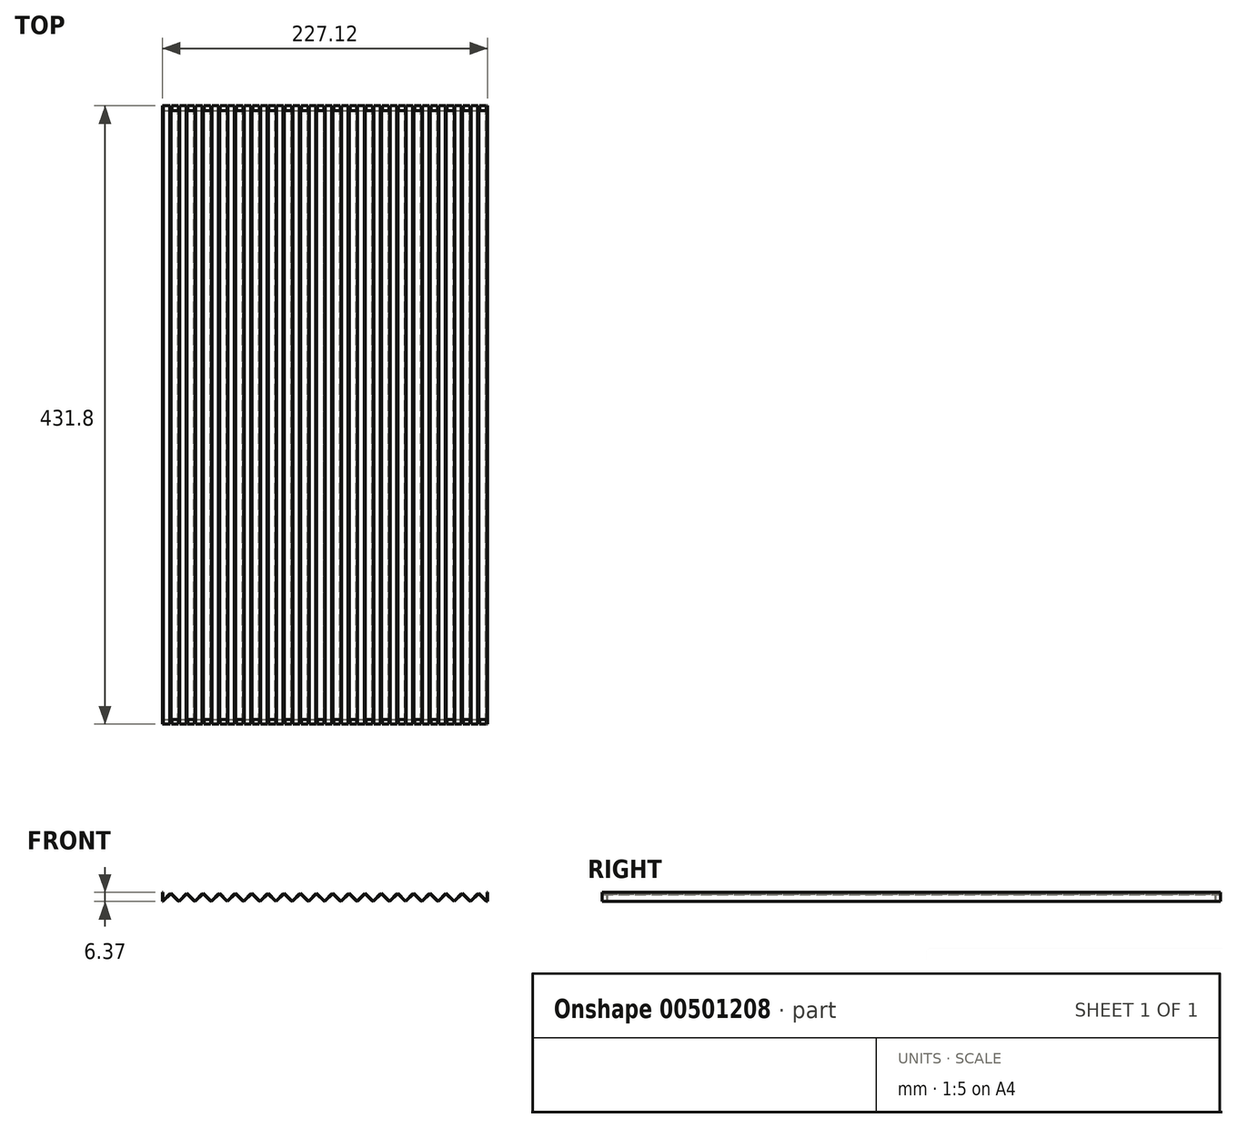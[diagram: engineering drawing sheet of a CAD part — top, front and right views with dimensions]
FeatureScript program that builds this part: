
annotation { "Feature Type Name" : "Feature", "Feature Type Description" : "" }
export const myFeature = defineFeature(function(context is Context, id is Id, definition is map)
    precondition{}
    {
        {
            assignVariable(context, id + "F0", {"variableType" : VariableType.LENGTH, "name" : "StripL", "lengthValue" : 431.8 * mm});
        }
        {
            var Q0;
            Q0=qCreatedBy(makeId("Front.planeOp"),FACE);
            var sketch = newSketch(context, id + "F1", { "sketchPlane" : qUnion([Q0])});
            skLineSegment(sketch, "E0", {"start": v(-11.31, 2.85) * mm, "end": v(0, 2.85) * mm, "construction": true});
            skLineSegment(sketch, "E1", {"start": v(-11.31, -2.85) * mm, "end": v(0, -2.85) * mm, "construction": true});
            skLineSegment(sketch, "E2", {"start": v(-11.31, -2.85) * mm, "end": v(-5.66, 2.81) * mm});
            skLineSegment(sketch, "E3", {"start": v(-5.66, 2.81) * mm, "end": v(0, -2.85) * mm});
            skLineSegment(sketch, "E4", {"start": v(-11.31, -2.81) * mm, "end": v(-5.66, 2.85) * mm});
            skLineSegment(sketch, "E5", {"start": v(-5.66, 2.85) * mm, "end": v(0, -2.81) * mm});
            skLineSegment(sketch, "E6.1.0.0", {"start": v(0, -2.81) * mm, "end": v(5.66, 2.85) * mm});
            skLineSegment(sketch, "E6.1.0.1", {"start": v(0, -2.85) * mm, "end": v(5.66, 2.81) * mm});
            skLineSegment(sketch, "E6.1.0.2", {"start": v(5.66, 2.81) * mm, "end": v(11.31, -2.85) * mm});
            skLineSegment(sketch, "E6.1.0.3", {"start": v(5.66, 2.85) * mm, "end": v(11.31, -2.81) * mm});
            skLineSegment(sketch, "E6.2.0.0", {"start": v(11.31, -2.81) * mm, "end": v(16.97, 2.85) * mm});
            skLineSegment(sketch, "E6.2.0.1", {"start": v(11.31, -2.85) * mm, "end": v(16.97, 2.81) * mm});
            skLineSegment(sketch, "E6.2.0.2", {"start": v(16.97, 2.81) * mm, "end": v(22.63, -2.85) * mm});
            skLineSegment(sketch, "E6.2.0.3", {"start": v(16.97, 2.85) * mm, "end": v(22.63, -2.81) * mm});
            skLineSegment(sketch, "E6.direction1", {"start": v(-11.31, -2.81) * mm, "end": v(0, -2.81) * mm, "construction": true});
            skLineSegment(sketch, "E7.0.3.0", {"start": v(22.63, -2.81) * mm, "end": v(28.28, 2.85) * mm});
            skLineSegment(sketch, "E7.3.3.0", {"start": v(22.63, -2.85) * mm, "end": v(28.28, 2.81) * mm});
            skLineSegment(sketch, "E7.6.3.0", {"start": v(28.28, 2.81) * mm, "end": v(33.94, -2.85) * mm});
            skLineSegment(sketch, "E7.9.3.0", {"start": v(28.28, 2.85) * mm, "end": v(33.94, -2.81) * mm});
            skLineSegment(sketch, "E7.0.4.0", {"start": v(33.94, -2.81) * mm, "end": v(39.6, 2.85) * mm});
            skLineSegment(sketch, "E7.3.4.0", {"start": v(33.94, -2.85) * mm, "end": v(39.6, 2.81) * mm});
            skLineSegment(sketch, "E7.6.4.0", {"start": v(39.6, 2.81) * mm, "end": v(45.25, -2.85) * mm});
            skLineSegment(sketch, "E7.9.4.0", {"start": v(39.6, 2.85) * mm, "end": v(45.25, -2.81) * mm});
            skLineSegment(sketch, "E8.0.5.0", {"start": v(45.25, -2.81) * mm, "end": v(50.91, 2.85) * mm});
            skLineSegment(sketch, "E8.3.5.0", {"start": v(45.25, -2.85) * mm, "end": v(50.91, 2.81) * mm});
            skLineSegment(sketch, "E8.6.5.0", {"start": v(50.91, 2.81) * mm, "end": v(56.57, -2.85) * mm});
            skLineSegment(sketch, "E8.9.5.0", {"start": v(50.91, 2.85) * mm, "end": v(56.57, -2.81) * mm});
            skLineSegment(sketch, "E9.0.6.0", {"start": v(56.57, -2.81) * mm, "end": v(62.23, 2.85) * mm});
            skLineSegment(sketch, "E9.3.6.0", {"start": v(56.57, -2.85) * mm, "end": v(62.23, 2.81) * mm});
            skLineSegment(sketch, "E9.6.6.0", {"start": v(62.23, 2.81) * mm, "end": v(67.88, -2.85) * mm});
            skLineSegment(sketch, "E9.9.6.0", {"start": v(62.23, 2.85) * mm, "end": v(67.88, -2.81) * mm});
            skLineSegment(sketch, "E9.0.7.0", {"start": v(67.88, -2.81) * mm, "end": v(73.54, 2.85) * mm});
            skLineSegment(sketch, "E9.3.7.0", {"start": v(67.88, -2.85) * mm, "end": v(73.54, 2.81) * mm});
            skLineSegment(sketch, "E9.6.7.0", {"start": v(73.54, 2.81) * mm, "end": v(79.2, -2.85) * mm});
            skLineSegment(sketch, "E9.9.7.0", {"start": v(73.54, 2.85) * mm, "end": v(79.2, -2.81) * mm});
            skLineSegment(sketch, "E10.0.8.0", {"start": v(79.2, -2.81) * mm, "end": v(84.85, 2.85) * mm});
            skLineSegment(sketch, "E10.3.8.0", {"start": v(79.2, -2.85) * mm, "end": v(84.85, 2.81) * mm});
            skLineSegment(sketch, "E10.6.8.0", {"start": v(84.85, 2.81) * mm, "end": v(90.5, -2.85) * mm});
            skLineSegment(sketch, "E10.9.8.0", {"start": v(84.85, 2.85) * mm, "end": v(90.5, -2.81) * mm});
            skLineSegment(sketch, "E10.0.9.0", {"start": v(90.5, -2.81) * mm, "end": v(96.17, 2.85) * mm});
            skLineSegment(sketch, "E10.3.9.0", {"start": v(90.5, -2.85) * mm, "end": v(96.17, 2.81) * mm});
            skLineSegment(sketch, "E10.6.9.0", {"start": v(96.17, 2.81) * mm, "end": v(101.82, -2.85) * mm});
            skLineSegment(sketch, "E10.9.9.0", {"start": v(96.17, 2.85) * mm, "end": v(101.82, -2.81) * mm});
            skLineSegment(sketch, "E10.0.10.0", {"start": v(101.82, -2.81) * mm, "end": v(107.48, 2.85) * mm});
            skLineSegment(sketch, "E10.3.10.0", {"start": v(101.82, -2.85) * mm, "end": v(107.48, 2.81) * mm});
            skLineSegment(sketch, "E10.6.10.0", {"start": v(107.48, 2.81) * mm, "end": v(113.14, -2.85) * mm});
            skLineSegment(sketch, "E10.9.10.0", {"start": v(107.48, 2.85) * mm, "end": v(113.14, -2.81) * mm});
            skLineSegment(sketch, "E10.0.11.0", {"start": v(113.14, -2.81) * mm, "end": v(118.8, 2.85) * mm});
            skLineSegment(sketch, "E10.3.11.0", {"start": v(113.14, -2.85) * mm, "end": v(118.8, 2.81) * mm});
            skLineSegment(sketch, "E10.6.11.0", {"start": v(118.8, 2.81) * mm, "end": v(124.45, -2.85) * mm});
            skLineSegment(sketch, "E10.9.11.0", {"start": v(118.8, 2.85) * mm, "end": v(124.45, -2.81) * mm});
            skLineSegment(sketch, "E10.0.12.0", {"start": v(124.45, -2.81) * mm, "end": v(130.1, 2.85) * mm});
            skLineSegment(sketch, "E10.3.12.0", {"start": v(124.45, -2.85) * mm, "end": v(130.1, 2.81) * mm});
            skLineSegment(sketch, "E10.6.12.0", {"start": v(130.1, 2.81) * mm, "end": v(135.76, -2.85) * mm});
            skLineSegment(sketch, "E10.9.12.0", {"start": v(130.1, 2.85) * mm, "end": v(135.76, -2.81) * mm});
            skLineSegment(sketch, "E10.0.13.0", {"start": v(135.76, -2.81) * mm, "end": v(141.42, 2.85) * mm});
            skLineSegment(sketch, "E10.3.13.0", {"start": v(135.76, -2.85) * mm, "end": v(141.42, 2.81) * mm});
            skLineSegment(sketch, "E10.6.13.0", {"start": v(141.42, 2.81) * mm, "end": v(147.08, -2.85) * mm});
            skLineSegment(sketch, "E10.9.13.0", {"start": v(141.42, 2.85) * mm, "end": v(147.08, -2.81) * mm});
            skLineSegment(sketch, "E10.0.14.0", {"start": v(147.08, -2.81) * mm, "end": v(152.74, 2.85) * mm});
            skLineSegment(sketch, "E10.3.14.0", {"start": v(147.08, -2.85) * mm, "end": v(152.74, 2.81) * mm});
            skLineSegment(sketch, "E10.6.14.0", {"start": v(152.74, 2.81) * mm, "end": v(158.4, -2.85) * mm});
            skLineSegment(sketch, "E10.9.14.0", {"start": v(152.74, 2.85) * mm, "end": v(158.4, -2.81) * mm});
            skLineSegment(sketch, "E10.0.15.0", {"start": v(158.4, -2.81) * mm, "end": v(164.05, 2.85) * mm});
            skLineSegment(sketch, "E10.3.15.0", {"start": v(158.4, -2.85) * mm, "end": v(164.05, 2.81) * mm});
            skLineSegment(sketch, "E10.6.15.0", {"start": v(164.05, 2.81) * mm, "end": v(169.7, -2.85) * mm});
            skLineSegment(sketch, "E10.9.15.0", {"start": v(164.05, 2.85) * mm, "end": v(169.7, -2.81) * mm});
            skLineSegment(sketch, "E10.0.16.0", {"start": v(169.7, -2.81) * mm, "end": v(175.36, 2.85) * mm});
            skLineSegment(sketch, "E10.3.16.0", {"start": v(169.7, -2.85) * mm, "end": v(175.36, 2.81) * mm});
            skLineSegment(sketch, "E10.6.16.0", {"start": v(175.36, 2.81) * mm, "end": v(181.02, -2.85) * mm});
            skLineSegment(sketch, "E10.9.16.0", {"start": v(175.36, 2.85) * mm, "end": v(181.02, -2.81) * mm});
            skLineSegment(sketch, "E10.0.17.0", {"start": v(181.02, -2.81) * mm, "end": v(186.68, 2.85) * mm});
            skLineSegment(sketch, "E10.3.17.0", {"start": v(181.02, -2.85) * mm, "end": v(186.68, 2.81) * mm});
            skLineSegment(sketch, "E10.6.17.0", {"start": v(186.68, 2.81) * mm, "end": v(192.33, -2.85) * mm});
            skLineSegment(sketch, "E10.9.17.0", {"start": v(186.68, 2.85) * mm, "end": v(192.33, -2.81) * mm});
            skLineSegment(sketch, "E10.0.18.0", {"start": v(192.33, -2.81) * mm, "end": v(197.99, 2.85) * mm});
            skLineSegment(sketch, "E10.3.18.0", {"start": v(192.33, -2.85) * mm, "end": v(197.99, 2.81) * mm});
            skLineSegment(sketch, "E10.6.18.0", {"start": v(197.99, 2.81) * mm, "end": v(203.65, -2.85) * mm});
            skLineSegment(sketch, "E10.9.18.0", {"start": v(197.99, 2.85) * mm, "end": v(203.65, -2.81) * mm});
            skLineSegment(sketch, "E10.0.19.0", {"start": v(203.65, -2.81) * mm, "end": v(209.3, 2.85) * mm});
            skLineSegment(sketch, "E10.3.19.0", {"start": v(203.65, -2.85) * mm, "end": v(209.3, 2.81) * mm});
            skLineSegment(sketch, "E10.6.19.0", {"start": v(209.3, 2.81) * mm, "end": v(214.96, -2.85) * mm});
            skLineSegment(sketch, "E10.9.19.0", {"start": v(209.3, 2.85) * mm, "end": v(214.96, -2.81) * mm});
            skLineSegment(sketch, "E11", {"start": v(-11.31, -2.81) * mm, "end": v(-11.31, 2.85) * mm});
            skLineSegment(sketch, "E12", {"start": v(-11.31, -2.85) * mm, "end": v(-11.33, -2.83) * mm});
            skLineSegment(sketch, "E13", {"start": v(-11.33, -2.83) * mm, "end": v(-11.33, 2.85) * mm});
            skLineSegment(sketch, "E14", {"start": v(-11.33, 2.85) * mm, "end": v(-11.31, 2.85) * mm});
            skLineSegment(sketch, "E15", {"start": v(214.96, -2.81) * mm, "end": v(214.96, 2.85) * mm});
            skLineSegment(sketch, "E16", {"start": v(214.96, -2.85) * mm, "end": v(214.98, -2.83) * mm});
            skLineSegment(sketch, "E17", {"start": v(214.98, -2.83) * mm, "end": v(214.98, 2.85) * mm});
            skLineSegment(sketch, "E18", {"start": v(214.98, 2.85) * mm, "end": v(214.96, 2.85) * mm});
            skSolve(sketch);
        }
        {
            var Q0;
            Q0 = qSketchRegion(id + "F1", true);
            extrude(context, id + "F2", {"entities" : qUnion([Q0]), "depth" : 425 * mm, "offsetDistance" : 25 * mm, "symmetric" : true});
        }
        {
            var Q0;
            Q0=qCreatedBy(makeId("Front.planeOp"),FACE);
            var sketch = newSketch(context, id + "F3", { "sketchPlane" : qUnion([Q0])});
            skLineSegment(sketch, "E19.0", {"start": v(-11.33, -2.83) * mm, "end": v(-11.33, 2.85) * mm});
            skLineSegment(sketch, "E19.1", {"start": v(-11.31, -2.81) * mm, "end": v(-5.66, 2.85) * mm});
            skLineSegment(sketch, "E19.2", {"start": v(-5.66, 2.81) * mm, "end": v(0, -2.85) * mm});
            skLineSegment(sketch, "E19.3", {"start": v(0, -2.81) * mm, "end": v(5.66, 2.85) * mm});
            skLineSegment(sketch, "E19.4", {"start": v(5.66, 2.81) * mm, "end": v(11.31, -2.85) * mm});
            skLineSegment(sketch, "E19.5", {"start": v(11.31, -2.81) * mm, "end": v(16.97, 2.85) * mm});
            skLineSegment(sketch, "E19.6", {"start": v(16.97, 2.81) * mm, "end": v(22.63, -2.85) * mm});
            skLineSegment(sketch, "E19.7", {"start": v(22.63, -2.81) * mm, "end": v(28.28, 2.85) * mm});
            skLineSegment(sketch, "E19.8", {"start": v(28.28, 2.81) * mm, "end": v(33.94, -2.85) * mm});
            skLineSegment(sketch, "E19.9", {"start": v(33.94, -2.81) * mm, "end": v(39.6, 2.85) * mm});
            skLineSegment(sketch, "E19.10", {"start": v(39.6, 2.81) * mm, "end": v(45.25, -2.85) * mm});
            skLineSegment(sketch, "E19.11", {"start": v(45.25, -2.81) * mm, "end": v(50.91, 2.85) * mm});
            skLineSegment(sketch, "E19.12", {"start": v(50.91, 2.81) * mm, "end": v(56.57, -2.85) * mm});
            skLineSegment(sketch, "E19.13", {"start": v(56.57, -2.81) * mm, "end": v(62.23, 2.85) * mm});
            skLineSegment(sketch, "E19.14", {"start": v(62.23, 2.81) * mm, "end": v(67.88, -2.85) * mm});
            skLineSegment(sketch, "E19.15", {"start": v(67.88, -2.81) * mm, "end": v(73.54, 2.85) * mm});
            skLineSegment(sketch, "E19.16", {"start": v(73.54, 2.81) * mm, "end": v(79.2, -2.85) * mm});
            skLineSegment(sketch, "E19.17", {"start": v(79.2, -2.81) * mm, "end": v(84.85, 2.85) * mm});
            skLineSegment(sketch, "E19.18", {"start": v(84.85, 2.81) * mm, "end": v(90.5, -2.85) * mm});
            skLineSegment(sketch, "E19.19", {"start": v(90.5, -2.81) * mm, "end": v(96.17, 2.85) * mm});
            skLineSegment(sketch, "E19.20", {"start": v(96.17, 2.81) * mm, "end": v(101.82, -2.85) * mm});
            skLineSegment(sketch, "E19.21", {"start": v(101.82, -2.81) * mm, "end": v(107.48, 2.85) * mm});
            skLineSegment(sketch, "E19.22", {"start": v(107.48, 2.81) * mm, "end": v(113.14, -2.85) * mm});
            skLineSegment(sketch, "E19.23", {"start": v(113.14, -2.81) * mm, "end": v(118.8, 2.85) * mm});
            skLineSegment(sketch, "E19.24", {"start": v(118.8, 2.81) * mm, "end": v(124.45, -2.85) * mm});
            skLineSegment(sketch, "E19.25", {"start": v(124.45, -2.81) * mm, "end": v(130.1, 2.85) * mm});
            skLineSegment(sketch, "E19.26", {"start": v(130.1, 2.81) * mm, "end": v(135.76, -2.85) * mm});
            skLineSegment(sketch, "E19.27", {"start": v(135.76, -2.81) * mm, "end": v(141.42, 2.85) * mm});
            skLineSegment(sketch, "E19.28", {"start": v(141.42, 2.81) * mm, "end": v(147.08, -2.85) * mm});
            skLineSegment(sketch, "E19.29", {"start": v(147.08, -2.81) * mm, "end": v(152.74, 2.85) * mm});
            skLineSegment(sketch, "E19.30", {"start": v(152.74, 2.81) * mm, "end": v(158.4, -2.85) * mm});
            skLineSegment(sketch, "E19.31", {"start": v(158.4, -2.81) * mm, "end": v(164.05, 2.85) * mm});
            skLineSegment(sketch, "E19.32", {"start": v(164.05, 2.81) * mm, "end": v(169.7, -2.85) * mm});
            skLineSegment(sketch, "E19.33", {"start": v(169.7, -2.81) * mm, "end": v(175.36, 2.85) * mm});
            skLineSegment(sketch, "E19.34", {"start": v(175.36, 2.81) * mm, "end": v(181.02, -2.85) * mm});
            skLineSegment(sketch, "E19.35", {"start": v(181.02, -2.81) * mm, "end": v(186.68, 2.85) * mm});
            skLineSegment(sketch, "E19.36", {"start": v(186.68, 2.81) * mm, "end": v(192.33, -2.85) * mm});
            skLineSegment(sketch, "E19.37", {"start": v(192.33, -2.81) * mm, "end": v(197.99, 2.85) * mm});
            skLineSegment(sketch, "E19.38", {"start": v(197.99, 2.81) * mm, "end": v(203.65, -2.85) * mm});
            skLineSegment(sketch, "E19.39", {"start": v(203.65, -2.81) * mm, "end": v(209.3, 2.85) * mm});
            skLineSegment(sketch, "E19.40", {"start": v(209.3, 2.81) * mm, "end": v(214.96, -2.85) * mm});
            skLineSegment(sketch, "E19.41", {"start": v(214.96, -2.81) * mm, "end": v(214.96, 2.85) * mm});
            skLineSegment(sketch, "E20", {"start": v(-10.73, -2.23) * mm, "end": v(-11.02, -1.94) * mm});
            skLineSegment(sketch, "E21", {"start": v(-11.02, -1.94) * mm, "end": v(-6.53, 2.55) * mm});
            skLineSegment(sketch, "E22", {"start": v(-6.53, 2.55) * mm, "end": v(-6.24, 2.26) * mm});
            skLineSegment(sketch, "E23", {"start": v(-8.77, 0.3) * mm, "end": v(-8.49, 0.02) * mm, "construction": true});
            skLineSegment(sketch, "E24", {"start": v(-5.07, 2.23) * mm, "end": v(-5.36, 1.94) * mm});
            skLineSegment(sketch, "E25", {"start": v(-5.36, 1.94) * mm, "end": v(-0.87, -2.55) * mm});
            skLineSegment(sketch, "E26", {"start": v(-0.87, -2.55) * mm, "end": v(-0.58, -2.26) * mm});
            skLineSegment(sketch, "E27", {"start": v(-3.12, -0.3) * mm, "end": v(-2.83, -0.02) * mm, "construction": true});
            skLineSegment(sketch, "E28.1.0.0", {"start": v(4.79, 2.55) * mm, "end": v(5.07, 2.26) * mm});
            skLineSegment(sketch, "E28.1.0.1", {"start": v(0.3, -1.94) * mm, "end": v(4.79, 2.55) * mm});
            skLineSegment(sketch, "E28.1.0.2", {"start": v(0.58, -2.23) * mm, "end": v(0.3, -1.94) * mm});
            skLineSegment(sketch, "E28.1.0.3", {"start": v(6.24, 2.23) * mm, "end": v(5.95, 1.94) * mm});
            skLineSegment(sketch, "E28.1.0.4", {"start": v(5.95, 1.94) * mm, "end": v(10.44, -2.55) * mm});
            skLineSegment(sketch, "E28.1.0.5", {"start": v(10.44, -2.55) * mm, "end": v(10.73, -2.26) * mm});
            skLineSegment(sketch, "E28.2.0.0", {"start": v(16.1, 2.55) * mm, "end": v(16.39, 2.26) * mm});
            skLineSegment(sketch, "E28.2.0.1", {"start": v(11.6, -1.94) * mm, "end": v(16.1, 2.55) * mm});
            skLineSegment(sketch, "E28.2.0.2", {"start": v(11.9, -2.23) * mm, "end": v(11.6, -1.94) * mm});
            skLineSegment(sketch, "E28.2.0.3", {"start": v(17.55, 2.23) * mm, "end": v(17.27, 1.94) * mm});
            skLineSegment(sketch, "E28.2.0.4", {"start": v(17.27, 1.94) * mm, "end": v(21.76, -2.55) * mm});
            skLineSegment(sketch, "E28.2.0.5", {"start": v(21.76, -2.55) * mm, "end": v(22.04, -2.26) * mm});
            skLineSegment(sketch, "E28.3.0.0", {"start": v(27.41, 2.55) * mm, "end": v(27.7, 2.26) * mm});
            skLineSegment(sketch, "E28.3.0.1", {"start": v(22.92, -1.94) * mm, "end": v(27.41, 2.55) * mm});
            skLineSegment(sketch, "E28.3.0.2", {"start": v(23.21, -2.23) * mm, "end": v(22.92, -1.94) * mm});
            skLineSegment(sketch, "E28.3.0.3", {"start": v(28.87, 2.23) * mm, "end": v(28.58, 1.94) * mm});
            skLineSegment(sketch, "E28.3.0.4", {"start": v(28.58, 1.94) * mm, "end": v(33.07, -2.55) * mm});
            skLineSegment(sketch, "E28.3.0.5", {"start": v(33.07, -2.55) * mm, "end": v(33.36, -2.26) * mm});
            skLineSegment(sketch, "E28.4.0.0", {"start": v(38.73, 2.55) * mm, "end": v(39.01, 2.26) * mm});
            skLineSegment(sketch, "E28.4.0.1", {"start": v(34.24, -1.94) * mm, "end": v(38.73, 2.55) * mm});
            skLineSegment(sketch, "E28.4.0.2", {"start": v(34.52, -2.23) * mm, "end": v(34.24, -1.94) * mm});
            skLineSegment(sketch, "E28.4.0.3", {"start": v(40.18, 2.23) * mm, "end": v(39.9, 1.94) * mm});
            skLineSegment(sketch, "E28.4.0.4", {"start": v(39.9, 1.94) * mm, "end": v(44.38, -2.55) * mm});
            skLineSegment(sketch, "E28.4.0.5", {"start": v(44.38, -2.55) * mm, "end": v(44.67, -2.26) * mm});
            skLineSegment(sketch, "E28.5.0.0", {"start": v(50.04, 2.55) * mm, "end": v(50.33, 2.26) * mm});
            skLineSegment(sketch, "E28.5.0.1", {"start": v(45.55, -1.94) * mm, "end": v(50.04, 2.55) * mm});
            skLineSegment(sketch, "E28.5.0.2", {"start": v(45.84, -2.23) * mm, "end": v(45.55, -1.94) * mm});
            skLineSegment(sketch, "E28.5.0.3", {"start": v(51.5, 2.23) * mm, "end": v(51.2, 1.94) * mm});
            skLineSegment(sketch, "E28.5.0.4", {"start": v(51.2, 1.94) * mm, "end": v(55.7, -2.55) * mm});
            skLineSegment(sketch, "E28.5.0.5", {"start": v(55.7, -2.55) * mm, "end": v(55.99, -2.26) * mm});
            skLineSegment(sketch, "E28.6.0.0", {"start": v(61.35, 2.55) * mm, "end": v(61.64, 2.26) * mm});
            skLineSegment(sketch, "E28.6.0.1", {"start": v(56.86, -1.94) * mm, "end": v(61.35, 2.55) * mm});
            skLineSegment(sketch, "E28.6.0.2", {"start": v(57.15, -2.23) * mm, "end": v(56.86, -1.94) * mm});
            skLineSegment(sketch, "E28.6.0.3", {"start": v(62.8, 2.23) * mm, "end": v(62.52, 1.94) * mm});
            skLineSegment(sketch, "E28.6.0.4", {"start": v(62.52, 1.94) * mm, "end": v(67.01, -2.55) * mm});
            skLineSegment(sketch, "E28.6.0.5", {"start": v(67.01, -2.55) * mm, "end": v(67.3, -2.26) * mm});
            skLineSegment(sketch, "E28.7.0.0", {"start": v(72.67, 2.55) * mm, "end": v(72.96, 2.26) * mm});
            skLineSegment(sketch, "E28.7.0.1", {"start": v(68.18, -1.94) * mm, "end": v(72.67, 2.55) * mm});
            skLineSegment(sketch, "E28.7.0.2", {"start": v(68.47, -2.23) * mm, "end": v(68.18, -1.94) * mm});
            skLineSegment(sketch, "E28.7.0.3", {"start": v(74.12, 2.23) * mm, "end": v(73.84, 1.94) * mm});
            skLineSegment(sketch, "E28.7.0.4", {"start": v(73.84, 1.94) * mm, "end": v(78.33, -2.55) * mm});
            skLineSegment(sketch, "E28.7.0.5", {"start": v(78.33, -2.55) * mm, "end": v(78.61, -2.26) * mm});
            skLineSegment(sketch, "E28.8.0.0", {"start": v(83.98, 2.55) * mm, "end": v(84.27, 2.26) * mm});
            skLineSegment(sketch, "E28.8.0.1", {"start": v(79.5, -1.94) * mm, "end": v(83.98, 2.55) * mm});
            skLineSegment(sketch, "E28.8.0.2", {"start": v(79.78, -2.23) * mm, "end": v(79.5, -1.94) * mm});
            skLineSegment(sketch, "E28.8.0.3", {"start": v(85.44, 2.23) * mm, "end": v(85.15, 1.94) * mm});
            skLineSegment(sketch, "E28.8.0.4", {"start": v(85.15, 1.94) * mm, "end": v(89.64, -2.55) * mm});
            skLineSegment(sketch, "E28.8.0.5", {"start": v(89.64, -2.55) * mm, "end": v(89.93, -2.26) * mm});
            skLineSegment(sketch, "E28.9.0.0", {"start": v(95.3, 2.55) * mm, "end": v(95.58, 2.26) * mm});
            skLineSegment(sketch, "E28.9.0.1", {"start": v(90.8, -1.94) * mm, "end": v(95.3, 2.55) * mm});
            skLineSegment(sketch, "E28.9.0.2", {"start": v(91.1, -2.23) * mm, "end": v(90.8, -1.94) * mm});
            skLineSegment(sketch, "E28.9.0.3", {"start": v(96.75, 2.23) * mm, "end": v(96.46, 1.94) * mm});
            skLineSegment(sketch, "E28.9.0.4", {"start": v(96.46, 1.94) * mm, "end": v(100.95, -2.55) * mm});
            skLineSegment(sketch, "E28.9.0.5", {"start": v(100.95, -2.55) * mm, "end": v(101.24, -2.26) * mm});
            skLineSegment(sketch, "E28.10.0.0", {"start": v(106.6, 2.55) * mm, "end": v(106.9, 2.26) * mm});
            skLineSegment(sketch, "E28.10.0.1", {"start": v(102.12, -1.94) * mm, "end": v(106.6, 2.55) * mm});
            skLineSegment(sketch, "E28.10.0.2", {"start": v(102.4, -2.23) * mm, "end": v(102.12, -1.94) * mm});
            skLineSegment(sketch, "E28.10.0.3", {"start": v(108.06, 2.23) * mm, "end": v(107.78, 1.94) * mm});
            skLineSegment(sketch, "E28.10.0.4", {"start": v(107.78, 1.94) * mm, "end": v(112.27, -2.55) * mm});
            skLineSegment(sketch, "E28.10.0.5", {"start": v(112.27, -2.55) * mm, "end": v(112.55, -2.26) * mm});
            skLineSegment(sketch, "E28.11.0.0", {"start": v(117.92, 2.55) * mm, "end": v(118.21, 2.26) * mm});
            skLineSegment(sketch, "E28.11.0.1", {"start": v(113.43, -1.94) * mm, "end": v(117.92, 2.55) * mm});
            skLineSegment(sketch, "E28.11.0.2", {"start": v(113.72, -2.23) * mm, "end": v(113.43, -1.94) * mm});
            skLineSegment(sketch, "E28.11.0.3", {"start": v(119.38, 2.23) * mm, "end": v(119.09, 1.94) * mm});
            skLineSegment(sketch, "E28.11.0.4", {"start": v(119.09, 1.94) * mm, "end": v(123.58, -2.55) * mm});
            skLineSegment(sketch, "E28.11.0.5", {"start": v(123.58, -2.55) * mm, "end": v(123.87, -2.26) * mm});
            skLineSegment(sketch, "E28.12.0.0", {"start": v(129.24, 2.55) * mm, "end": v(129.52, 2.26) * mm});
            skLineSegment(sketch, "E28.12.0.1", {"start": v(124.75, -1.94) * mm, "end": v(129.24, 2.55) * mm});
            skLineSegment(sketch, "E28.12.0.2", {"start": v(125.03, -2.23) * mm, "end": v(124.75, -1.94) * mm});
            skLineSegment(sketch, "E28.12.0.3", {"start": v(130.7, 2.23) * mm, "end": v(130.4, 1.94) * mm});
            skLineSegment(sketch, "E28.12.0.4", {"start": v(130.4, 1.94) * mm, "end": v(134.9, -2.55) * mm});
            skLineSegment(sketch, "E28.12.0.5", {"start": v(134.9, -2.55) * mm, "end": v(135.18, -2.26) * mm});
            skLineSegment(sketch, "E28.13.0.0", {"start": v(140.55, 2.55) * mm, "end": v(140.84, 2.26) * mm});
            skLineSegment(sketch, "E28.13.0.1", {"start": v(136.06, -1.94) * mm, "end": v(140.55, 2.55) * mm});
            skLineSegment(sketch, "E28.13.0.2", {"start": v(136.35, -2.23) * mm, "end": v(136.06, -1.94) * mm});
            skLineSegment(sketch, "E28.13.0.3", {"start": v(142, 2.23) * mm, "end": v(141.72, 1.94) * mm});
            skLineSegment(sketch, "E28.13.0.4", {"start": v(141.72, 1.94) * mm, "end": v(146.2, -2.55) * mm});
            skLineSegment(sketch, "E28.13.0.5", {"start": v(146.2, -2.55) * mm, "end": v(146.5, -2.26) * mm});
            skLineSegment(sketch, "E28.14.0.0", {"start": v(151.86, 2.55) * mm, "end": v(152.15, 2.26) * mm});
            skLineSegment(sketch, "E28.14.0.1", {"start": v(147.37, -1.94) * mm, "end": v(151.86, 2.55) * mm});
            skLineSegment(sketch, "E28.14.0.2", {"start": v(147.66, -2.23) * mm, "end": v(147.37, -1.94) * mm});
            skLineSegment(sketch, "E28.14.0.3", {"start": v(153.32, 2.23) * mm, "end": v(153.03, 1.94) * mm});
            skLineSegment(sketch, "E28.14.0.4", {"start": v(153.03, 1.94) * mm, "end": v(157.52, -2.55) * mm});
            skLineSegment(sketch, "E28.14.0.5", {"start": v(157.52, -2.55) * mm, "end": v(157.8, -2.26) * mm});
            skLineSegment(sketch, "E28.15.0.0", {"start": v(163.18, 2.55) * mm, "end": v(163.47, 2.26) * mm});
            skLineSegment(sketch, "E28.15.0.1", {"start": v(158.69, -1.94) * mm, "end": v(163.18, 2.55) * mm});
            skLineSegment(sketch, "E28.15.0.2", {"start": v(158.98, -2.23) * mm, "end": v(158.69, -1.94) * mm});
            skLineSegment(sketch, "E28.15.0.3", {"start": v(164.63, 2.23) * mm, "end": v(164.34, 1.94) * mm});
            skLineSegment(sketch, "E28.15.0.4", {"start": v(164.34, 1.94) * mm, "end": v(168.83, -2.55) * mm});
            skLineSegment(sketch, "E28.15.0.5", {"start": v(168.83, -2.55) * mm, "end": v(169.12, -2.26) * mm});
            skLineSegment(sketch, "E28.16.0.0", {"start": v(174.5, 2.55) * mm, "end": v(174.78, 2.26) * mm});
            skLineSegment(sketch, "E28.16.0.1", {"start": v(170, -1.94) * mm, "end": v(174.5, 2.55) * mm});
            skLineSegment(sketch, "E28.16.0.2", {"start": v(170.29, -2.23) * mm, "end": v(170, -1.94) * mm});
            skLineSegment(sketch, "E28.16.0.3", {"start": v(175.95, 2.23) * mm, "end": v(175.66, 1.94) * mm});
            skLineSegment(sketch, "E28.16.0.4", {"start": v(175.66, 1.94) * mm, "end": v(180.15, -2.55) * mm});
            skLineSegment(sketch, "E28.16.0.5", {"start": v(180.15, -2.55) * mm, "end": v(180.44, -2.26) * mm});
            skLineSegment(sketch, "E28.17.0.0", {"start": v(185.8, 2.55) * mm, "end": v(186.1, 2.26) * mm});
            skLineSegment(sketch, "E28.17.0.1", {"start": v(181.32, -1.94) * mm, "end": v(185.8, 2.55) * mm});
            skLineSegment(sketch, "E28.17.0.2", {"start": v(181.6, -2.23) * mm, "end": v(181.32, -1.94) * mm});
            skLineSegment(sketch, "E28.17.0.3", {"start": v(187.26, 2.23) * mm, "end": v(186.97, 1.94) * mm});
            skLineSegment(sketch, "E28.17.0.4", {"start": v(186.97, 1.94) * mm, "end": v(191.46, -2.55) * mm});
            skLineSegment(sketch, "E28.17.0.5", {"start": v(191.46, -2.55) * mm, "end": v(191.75, -2.26) * mm});
            skLineSegment(sketch, "E28.18.0.0", {"start": v(197.12, 2.55) * mm, "end": v(197.4, 2.26) * mm});
            skLineSegment(sketch, "E28.18.0.1", {"start": v(192.63, -1.94) * mm, "end": v(197.12, 2.55) * mm});
            skLineSegment(sketch, "E28.18.0.2", {"start": v(192.92, -2.23) * mm, "end": v(192.63, -1.94) * mm});
            skLineSegment(sketch, "E28.18.0.3", {"start": v(198.57, 2.23) * mm, "end": v(198.29, 1.94) * mm});
            skLineSegment(sketch, "E28.18.0.4", {"start": v(198.29, 1.94) * mm, "end": v(202.78, -2.55) * mm});
            skLineSegment(sketch, "E28.18.0.5", {"start": v(202.78, -2.55) * mm, "end": v(203.06, -2.26) * mm});
            skLineSegment(sketch, "E28.19.0.0", {"start": v(208.43, 2.55) * mm, "end": v(208.72, 2.26) * mm});
            skLineSegment(sketch, "E28.19.0.1", {"start": v(203.94, -1.94) * mm, "end": v(208.43, 2.55) * mm});
            skLineSegment(sketch, "E28.19.0.2", {"start": v(204.23, -2.23) * mm, "end": v(203.94, -1.94) * mm});
            skLineSegment(sketch, "E28.19.0.3", {"start": v(209.89, 2.23) * mm, "end": v(209.6, 1.94) * mm});
            skLineSegment(sketch, "E28.19.0.4", {"start": v(209.6, 1.94) * mm, "end": v(214.09, -2.55) * mm});
            skLineSegment(sketch, "E28.19.0.5", {"start": v(214.09, -2.55) * mm, "end": v(214.38, -2.26) * mm});
            skLineSegment(sketch, "E28.direction1", {"start": v(-6.24, 2.26) * mm, "end": v(5.07, 2.26) * mm, "construction": true});
            skLineSegment(sketch, "E29", {"start": v(-11.33, 3.52) * mm, "end": v(-11.74, 3.52) * mm});
            skLineSegment(sketch, "E30", {"start": v(-11.74, 3.52) * mm, "end": v(-11.74, -2.83) * mm});
            skLineSegment(sketch, "E31", {"start": v(-11.74, -2.83) * mm, "end": v(-11.33, -2.83) * mm});
            skLineSegment(sketch, "E32", {"start": v(-11.33, 3.52) * mm, "end": v(-11.33, 2.85) * mm});
            skLineSegment(sketch, "E33.0", {"start": v(214.98, -2.83) * mm, "end": v(214.98, 2.85) * mm});
            skLineSegment(sketch, "E34", {"start": v(214.98, -2.83) * mm, "end": v(215.38, -2.83) * mm});
            skLineSegment(sketch, "E35", {"start": v(215.38, -2.83) * mm, "end": v(215.38, 3.52) * mm});
            skLineSegment(sketch, "E36", {"start": v(215.38, 3.52) * mm, "end": v(214.98, 3.52) * mm});
            skLineSegment(sketch, "E37", {"start": v(214.98, 3.52) * mm, "end": v(214.98, 2.85) * mm});
            skSolve(sketch);
        }
        {
            var Q0;
            Q0=makeQuery(id+"F3.imprint","IMPRINT",FACE,{"disambiguationData":[TD([[makeQuery(id+"F3.imprint","IMPRINT",EDGE,{"derivedFrom":sQuery(id+"F3.wireOp",EDGE,"E19.0")}),1.0]])]});
            var Q1;
            {var subQ0=sQuery(id+"F3.wireOp",EDGE,"E20");Q1=makeQuery(id+"F3.imprint","IMPRINT",FACE,{"disambiguationData":[TD([[makeQuery(id+"F3.imprint","IMPRINT",EDGE,{"derivedFrom":subQ0}),-1.0]])]});}
            var Q2;
            {var subQ0=sQuery(id+"F3.wireOp",EDGE,"E24");Q2=makeQuery(id+"F3.imprint","IMPRINT",FACE,{"disambiguationData":[TD([[makeQuery(id+"F3.imprint","IMPRINT",EDGE,{"derivedFrom":subQ0}),1.0]])]});}
            var Q3;
            {var subQ2=sQuery(id+"F3.wireOp",EDGE,"E28.1.0.0");Q3=makeQuery(id+"F3.imprint","IMPRINT",FACE,{"disambiguationData":[TD([[makeQuery(id+"F3.imprint","IMPRINT",EDGE,{"derivedFrom":subQ2}),-1.0]])]});}
            var Q4;
            {var subQ0=sQuery(id+"F3.wireOp",EDGE,"E28.1.0.3");Q4=makeQuery(id+"F3.imprint","IMPRINT",FACE,{"disambiguationData":[TD([[makeQuery(id+"F3.imprint","IMPRINT",EDGE,{"derivedFrom":subQ0}),1.0]])]});}
            var Q5;
            {var subQ2=sQuery(id+"F3.wireOp",EDGE,"E28.2.0.0");Q5=makeQuery(id+"F3.imprint","IMPRINT",FACE,{"disambiguationData":[TD([[makeQuery(id+"F3.imprint","IMPRINT",EDGE,{"derivedFrom":subQ2}),-1.0]])]});}
            var Q6;
            {var subQ0=sQuery(id+"F3.wireOp",EDGE,"E28.2.0.3");Q6=makeQuery(id+"F3.imprint","IMPRINT",FACE,{"disambiguationData":[TD([[makeQuery(id+"F3.imprint","IMPRINT",EDGE,{"derivedFrom":subQ0}),1.0]])]});}
            var Q7;
            {var subQ2=sQuery(id+"F3.wireOp",EDGE,"E28.3.0.0");Q7=makeQuery(id+"F3.imprint","IMPRINT",FACE,{"disambiguationData":[TD([[makeQuery(id+"F3.imprint","IMPRINT",EDGE,{"derivedFrom":subQ2}),-1.0]])]});}
            var Q8;
            {var subQ0=sQuery(id+"F3.wireOp",EDGE,"E28.3.0.3");Q8=makeQuery(id+"F3.imprint","IMPRINT",FACE,{"disambiguationData":[TD([[makeQuery(id+"F3.imprint","IMPRINT",EDGE,{"derivedFrom":subQ0}),1.0]])]});}
            var Q9;
            {var subQ2=sQuery(id+"F3.wireOp",EDGE,"E28.4.0.0");Q9=makeQuery(id+"F3.imprint","IMPRINT",FACE,{"disambiguationData":[TD([[makeQuery(id+"F3.imprint","IMPRINT",EDGE,{"derivedFrom":subQ2}),-1.0]])]});}
            var Q10;
            {var subQ0=sQuery(id+"F3.wireOp",EDGE,"E28.4.0.3");Q10=makeQuery(id+"F3.imprint","IMPRINT",FACE,{"disambiguationData":[TD([[makeQuery(id+"F3.imprint","IMPRINT",EDGE,{"derivedFrom":subQ0}),1.0]])]});}
            var Q11;
            {var subQ2=sQuery(id+"F3.wireOp",EDGE,"E28.5.0.0");Q11=makeQuery(id+"F3.imprint","IMPRINT",FACE,{"disambiguationData":[TD([[makeQuery(id+"F3.imprint","IMPRINT",EDGE,{"derivedFrom":subQ2}),-1.0]])]});}
            var Q12;
            {var subQ0=sQuery(id+"F3.wireOp",EDGE,"E28.5.0.3");Q12=makeQuery(id+"F3.imprint","IMPRINT",FACE,{"disambiguationData":[TD([[makeQuery(id+"F3.imprint","IMPRINT",EDGE,{"derivedFrom":subQ0}),1.0]])]});}
            var Q13;
            {var subQ2=sQuery(id+"F3.wireOp",EDGE,"E28.6.0.0");Q13=makeQuery(id+"F3.imprint","IMPRINT",FACE,{"disambiguationData":[TD([[makeQuery(id+"F3.imprint","IMPRINT",EDGE,{"derivedFrom":subQ2}),-1.0]])]});}
            var Q14;
            {var subQ0=sQuery(id+"F3.wireOp",EDGE,"E28.6.0.3");Q14=makeQuery(id+"F3.imprint","IMPRINT",FACE,{"disambiguationData":[TD([[makeQuery(id+"F3.imprint","IMPRINT",EDGE,{"derivedFrom":subQ0}),1.0]])]});}
            var Q15;
            {var subQ2=sQuery(id+"F3.wireOp",EDGE,"E28.7.0.0");Q15=makeQuery(id+"F3.imprint","IMPRINT",FACE,{"disambiguationData":[TD([[makeQuery(id+"F3.imprint","IMPRINT",EDGE,{"derivedFrom":subQ2}),-1.0]])]});}
            var Q16;
            {var subQ0=sQuery(id+"F3.wireOp",EDGE,"E28.7.0.3");Q16=makeQuery(id+"F3.imprint","IMPRINT",FACE,{"disambiguationData":[TD([[makeQuery(id+"F3.imprint","IMPRINT",EDGE,{"derivedFrom":subQ0}),1.0]])]});}
            var Q17;
            {var subQ2=sQuery(id+"F3.wireOp",EDGE,"E28.8.0.0");Q17=makeQuery(id+"F3.imprint","IMPRINT",FACE,{"disambiguationData":[TD([[makeQuery(id+"F3.imprint","IMPRINT",EDGE,{"derivedFrom":subQ2}),-1.0]])]});}
            var Q18;
            {var subQ0=sQuery(id+"F3.wireOp",EDGE,"E28.8.0.3");Q18=makeQuery(id+"F3.imprint","IMPRINT",FACE,{"disambiguationData":[TD([[makeQuery(id+"F3.imprint","IMPRINT",EDGE,{"derivedFrom":subQ0}),1.0]])]});}
            var Q19;
            {var subQ2=sQuery(id+"F3.wireOp",EDGE,"E28.9.0.0");Q19=makeQuery(id+"F3.imprint","IMPRINT",FACE,{"disambiguationData":[TD([[makeQuery(id+"F3.imprint","IMPRINT",EDGE,{"derivedFrom":subQ2}),-1.0]])]});}
            var Q20;
            {var subQ0=sQuery(id+"F3.wireOp",EDGE,"E28.9.0.3");Q20=makeQuery(id+"F3.imprint","IMPRINT",FACE,{"disambiguationData":[TD([[makeQuery(id+"F3.imprint","IMPRINT",EDGE,{"derivedFrom":subQ0}),1.0]])]});}
            var Q21;
            {var subQ2=sQuery(id+"F3.wireOp",EDGE,"E28.10.0.0");Q21=makeQuery(id+"F3.imprint","IMPRINT",FACE,{"disambiguationData":[TD([[makeQuery(id+"F3.imprint","IMPRINT",EDGE,{"derivedFrom":subQ2}),-1.0]])]});}
            var Q22;
            {var subQ0=sQuery(id+"F3.wireOp",EDGE,"E28.10.0.3");Q22=makeQuery(id+"F3.imprint","IMPRINT",FACE,{"disambiguationData":[TD([[makeQuery(id+"F3.imprint","IMPRINT",EDGE,{"derivedFrom":subQ0}),1.0]])]});}
            var Q23;
            {var subQ2=sQuery(id+"F3.wireOp",EDGE,"E28.11.0.0");Q23=makeQuery(id+"F3.imprint","IMPRINT",FACE,{"disambiguationData":[TD([[makeQuery(id+"F3.imprint","IMPRINT",EDGE,{"derivedFrom":subQ2}),-1.0]])]});}
            var Q24;
            {var subQ0=sQuery(id+"F3.wireOp",EDGE,"E28.11.0.3");Q24=makeQuery(id+"F3.imprint","IMPRINT",FACE,{"disambiguationData":[TD([[makeQuery(id+"F3.imprint","IMPRINT",EDGE,{"derivedFrom":subQ0}),1.0]])]});}
            var Q25;
            {var subQ2=sQuery(id+"F3.wireOp",EDGE,"E28.12.0.0");Q25=makeQuery(id+"F3.imprint","IMPRINT",FACE,{"disambiguationData":[TD([[makeQuery(id+"F3.imprint","IMPRINT",EDGE,{"derivedFrom":subQ2}),-1.0]])]});}
            var Q26;
            {var subQ0=sQuery(id+"F3.wireOp",EDGE,"E28.12.0.3");Q26=makeQuery(id+"F3.imprint","IMPRINT",FACE,{"disambiguationData":[TD([[makeQuery(id+"F3.imprint","IMPRINT",EDGE,{"derivedFrom":subQ0}),1.0]])]});}
            var Q27;
            {var subQ2=sQuery(id+"F3.wireOp",EDGE,"E28.13.0.0");Q27=makeQuery(id+"F3.imprint","IMPRINT",FACE,{"disambiguationData":[TD([[makeQuery(id+"F3.imprint","IMPRINT",EDGE,{"derivedFrom":subQ2}),-1.0]])]});}
            var Q28;
            {var subQ0=sQuery(id+"F3.wireOp",EDGE,"E28.13.0.3");Q28=makeQuery(id+"F3.imprint","IMPRINT",FACE,{"disambiguationData":[TD([[makeQuery(id+"F3.imprint","IMPRINT",EDGE,{"derivedFrom":subQ0}),1.0]])]});}
            var Q29;
            {var subQ2=sQuery(id+"F3.wireOp",EDGE,"E28.14.0.0");Q29=makeQuery(id+"F3.imprint","IMPRINT",FACE,{"disambiguationData":[TD([[makeQuery(id+"F3.imprint","IMPRINT",EDGE,{"derivedFrom":subQ2}),-1.0]])]});}
            var Q30;
            {var subQ0=sQuery(id+"F3.wireOp",EDGE,"E28.14.0.3");Q30=makeQuery(id+"F3.imprint","IMPRINT",FACE,{"disambiguationData":[TD([[makeQuery(id+"F3.imprint","IMPRINT",EDGE,{"derivedFrom":subQ0}),1.0]])]});}
            var Q31;
            {var subQ2=sQuery(id+"F3.wireOp",EDGE,"E28.15.0.0");Q31=makeQuery(id+"F3.imprint","IMPRINT",FACE,{"disambiguationData":[TD([[makeQuery(id+"F3.imprint","IMPRINT",EDGE,{"derivedFrom":subQ2}),-1.0]])]});}
            var Q32;
            {var subQ0=sQuery(id+"F3.wireOp",EDGE,"E28.15.0.3");Q32=makeQuery(id+"F3.imprint","IMPRINT",FACE,{"disambiguationData":[TD([[makeQuery(id+"F3.imprint","IMPRINT",EDGE,{"derivedFrom":subQ0}),1.0]])]});}
            var Q33;
            {var subQ2=sQuery(id+"F3.wireOp",EDGE,"E28.16.0.0");Q33=makeQuery(id+"F3.imprint","IMPRINT",FACE,{"disambiguationData":[TD([[makeQuery(id+"F3.imprint","IMPRINT",EDGE,{"derivedFrom":subQ2}),-1.0]])]});}
            var Q34;
            {var subQ0=sQuery(id+"F3.wireOp",EDGE,"E28.16.0.3");Q34=makeQuery(id+"F3.imprint","IMPRINT",FACE,{"disambiguationData":[TD([[makeQuery(id+"F3.imprint","IMPRINT",EDGE,{"derivedFrom":subQ0}),1.0]])]});}
            var Q35;
            {var subQ2=sQuery(id+"F3.wireOp",EDGE,"E28.17.0.0");Q35=makeQuery(id+"F3.imprint","IMPRINT",FACE,{"disambiguationData":[TD([[makeQuery(id+"F3.imprint","IMPRINT",EDGE,{"derivedFrom":subQ2}),-1.0]])]});}
            var Q36;
            {var subQ0=sQuery(id+"F3.wireOp",EDGE,"E28.17.0.3");Q36=makeQuery(id+"F3.imprint","IMPRINT",FACE,{"disambiguationData":[TD([[makeQuery(id+"F3.imprint","IMPRINT",EDGE,{"derivedFrom":subQ0}),1.0]])]});}
            var Q37;
            {var subQ2=sQuery(id+"F3.wireOp",EDGE,"E28.18.0.0");Q37=makeQuery(id+"F3.imprint","IMPRINT",FACE,{"disambiguationData":[TD([[makeQuery(id+"F3.imprint","IMPRINT",EDGE,{"derivedFrom":subQ2}),-1.0]])]});}
            var Q38;
            {var subQ0=sQuery(id+"F3.wireOp",EDGE,"E28.18.0.3");Q38=makeQuery(id+"F3.imprint","IMPRINT",FACE,{"disambiguationData":[TD([[makeQuery(id+"F3.imprint","IMPRINT",EDGE,{"derivedFrom":subQ0}),1.0]])]});}
            var Q39;
            {var subQ2=sQuery(id+"F3.wireOp",EDGE,"E28.19.0.0");Q39=makeQuery(id+"F3.imprint","IMPRINT",FACE,{"disambiguationData":[TD([[makeQuery(id+"F3.imprint","IMPRINT",EDGE,{"derivedFrom":subQ2}),-1.0]])]});}
            var Q40;
            {var subQ0=sQuery(id+"F3.wireOp",EDGE,"E28.19.0.3");Q40=makeQuery(id+"F3.imprint","IMPRINT",FACE,{"disambiguationData":[TD([[makeQuery(id+"F3.imprint","IMPRINT",EDGE,{"derivedFrom":subQ0}),1.0]])]});}
            var Q41;
            Q41=makeQuery(id+"F3.imprint","IMPRINT",FACE,{"disambiguationData":[TD([[makeQuery(id+"F3.imprint","IMPRINT",EDGE,{"derivedFrom":sQuery(id+"F3.wireOp",EDGE,"E33.0")}),-1.0]])]});
            extrude(context, id + "F4", {"entities" : qUnion([Q0, Q1, Q2, Q3, Q4, Q5, Q6, Q7, Q8, Q9, Q10, Q11, Q12, Q13, Q14, Q15, Q16, Q17, Q18, Q19, Q20, Q21, Q22, Q23, Q24, Q25, Q26, Q27, Q28, Q29, Q30, Q31, Q32, Q33, Q34, Q35, Q36, Q37, Q38, Q39, Q40, Q41]), "operationType" : NewBodyOperationType.ADD, "depth" : getVariable(context, 'StripL'), "offsetDistance" : 25 * mm, "symmetric" : true});
        }
    });
